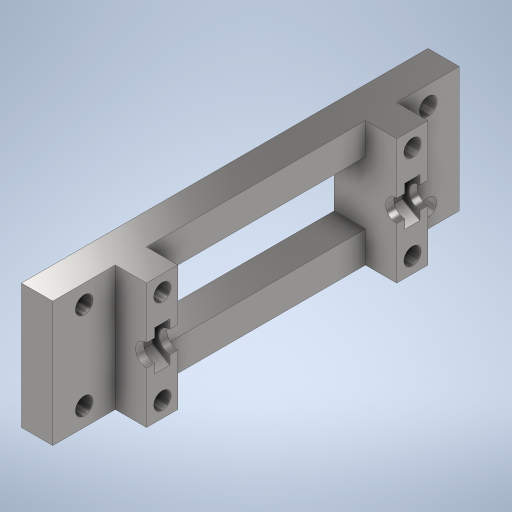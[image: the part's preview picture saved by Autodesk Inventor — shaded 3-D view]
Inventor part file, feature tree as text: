
AUTODESK INVENTOR PART (.ipt)
format: ipt  version: 2023 (Build 270158000, 158)  size: 389,120 bytes
history: native  units: mm
features: extrude x7, sketch x7, plane x2, mirror x1
ambient origin geometry x8: Origin, YZ Plane, XZ Plane, XY Plane, X Axis, Y Axis, Z Axis, Center Point
bodies: Solid1 (feature_tree)
feature tree (17):
  extrude  "Extrusion1"  Depth=5.0mm
  extrude  "Extrusion2"  Depth=15.0mm
  extrude  "Extrusion3"  Depth=35.0mm
  extrude  "Extrusion4"  Depth=10.0mm
  extrude  "Extrusion5"  Depth=10.0mm
  extrude  "Extrusion6"  Depth=200.0mm TaperAngle=0.0deg
  plane  "Work Plane1"
  extrude  "Extrusion7"  Depth=5.0mm
  plane  "Work Plane2"
  mirror  "Mirror1"
  sketch  "Sketch1"  dims[d0=5.0mm d1=5.0mm]
  sketch  "Sketch2"  dims[d2=5.0mm d3=15.0mm]
  sketch  "Sketch3"  dims[d4=15.0mm d5=35.0mm]
  sketch  "Sketch4"  dims[d6=20.0mm d7=0.0mm d8=10.0mm]
  sketch  "Sketch5"  dims[d9=10.0mm d10=10.0mm]
  sketch  "Sketch6"  dims[d11=3.5mm d12=200.0mm d13=0.0mm]
  sketch  "Sketch7"  dims[d14=5.0mm d15=5.0mm d16=20.0mm d17=0.0mm d18=10.0mm d19=10.0mm d20=3.0mm d21=3.0mm d22=5.0mm d23=5.0mm d24=5.0mm d25=5.0mm d26=3.0mm d27=3.0mm d28=2.75mm d29=2.75mm d30=2.75mm d31=2.75mm d32=5.0mm d33=0.0mm d34=2.5mm d35=2.5mm d36=2.5mm d37=2.5mm d38=2.5mm d39=2.5mm d40=2.5mm d41=2.5mm d42=2.7mm d43=2.7mm d44=2.7mm d45=2.7mm d46=15.0mm d47=0.0mm d48=4.7mm d49=4.7mm d50=4.7mm d51=4.7mm d52=7.5mm d53=0.0mm d57=20.0mm d58=2.4mm d59=0.0mm d60=2.75mm]
